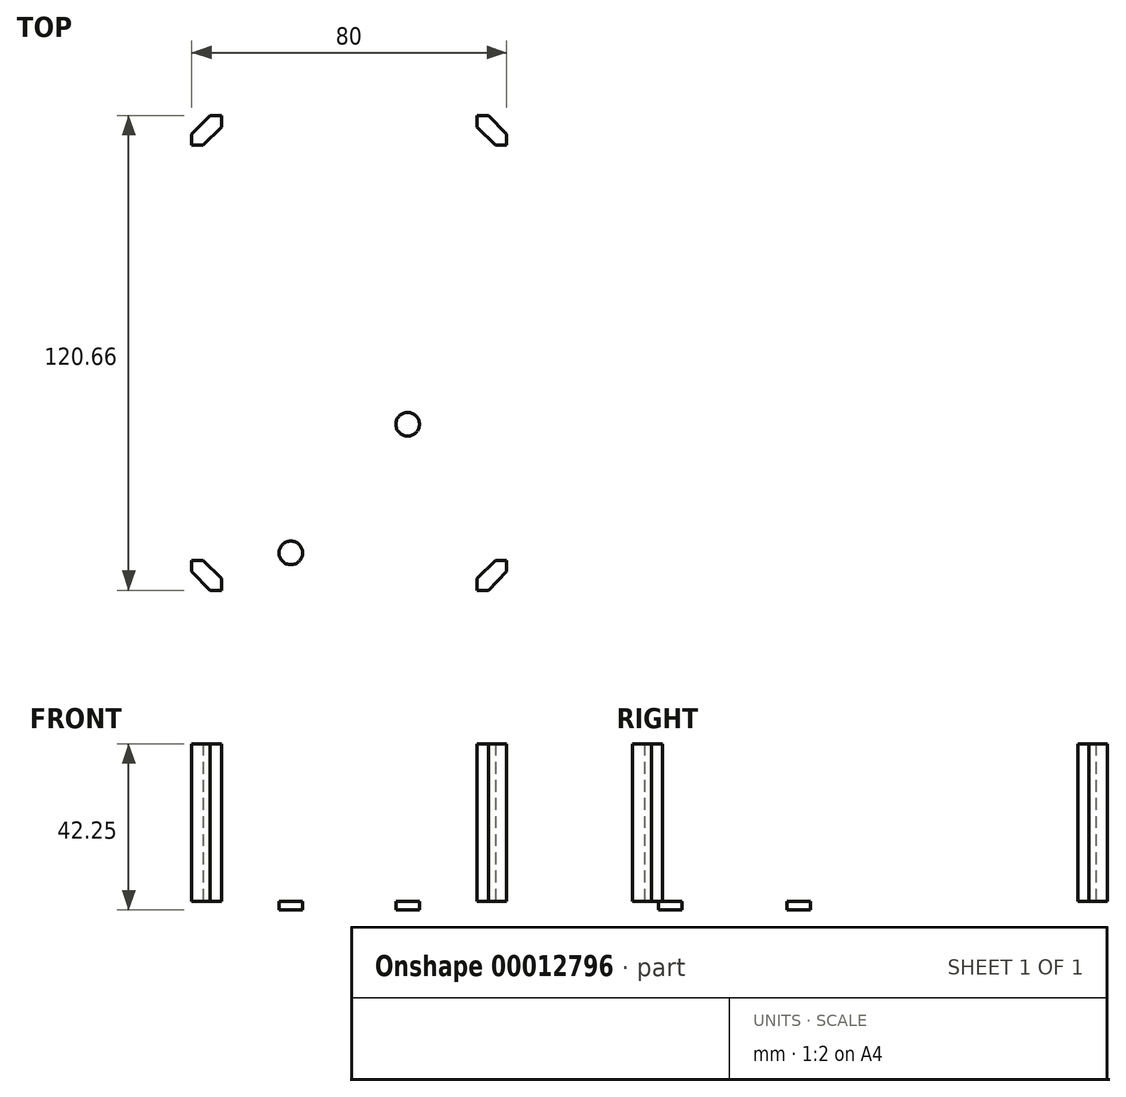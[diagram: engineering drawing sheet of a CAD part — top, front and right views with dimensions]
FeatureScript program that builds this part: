
annotation { "Feature Type Name" : "Feature", "Feature Type Description" : "" }
export const myFeature = defineFeature(function(context is Context, id is Id, definition is map)
    precondition{}
    {
        {
            var Q0;
            Q0=qCreatedBy(makeId("Top.planeOp"),FACE);
            var sketch = newSketch(context, id + "F0", { "sketchPlane" : qUnion([Q0])});
            skLineSegment(sketch, "E0.rect.bottom", {"start": v(-40, -60.33) * mm, "end": v(40, -60.33) * mm});
            skLineSegment(sketch, "E0.rect.top", {"start": v(-40, 60.33) * mm, "end": v(40, 60.33) * mm});
            skLineSegment(sketch, "E0.rect.left", {"start": v(-40, -60.33) * mm, "end": v(-40, 60.33) * mm});
            skLineSegment(sketch, "E0.rect.right", {"start": v(40, -60.33) * mm, "end": v(40, 60.33) * mm});
            skPoint(sketch, "E0.rect.middle", {"position": v(0, 0) * mm});
            skLineSegment(sketch, "E1", {"start": v(-35.41, 60.33) * mm, "end": v(-40, 55.6) * mm});
            skLineSegment(sketch, "E2", {"start": v(-35.22, -60.32) * mm, "end": v(-40, -55.8) * mm});
            skLineSegment(sketch, "E3.0.MirrorCS", {"start": v(35.22, -60.32) * mm, "end": v(40, -55.8) * mm});
            skLineSegment(sketch, "E4.0.MirrorCS", {"start": v(35.41, 60.33) * mm, "end": v(40, 55.6) * mm});
            skSolve(sketch);
        }
        {
            var Q0;
            {var subQ3=sQuery(id+"F0.wireOp",EDGE,"E1");Q0=makeQuery(id+"F0.imprint","IMPRINT",FACE,{"disambiguationData":[TD([[makeQuery(id+"F0.imprint","IMPRINT",EDGE,{"derivedFrom":subQ3}),1.0]])]});}
            extrude(context, id + "F1", {"entities" : qUnion([Q0]), "depth" : 2.25 * mm});
        }
        {
            var Q0;
            Q0=makeQuery(id+"F1.opExtrude","CAP_FACE",FACE,{"disambiguationData":[OSD([sQuery(id+"F0.wireOp",EDGE,"E0.rect.bottom"),sQuery(id+"F0.wireOp",EDGE,"E0.rect.top"),sQuery(id+"F0.wireOp",EDGE,"E0.rect.left"),sQuery(id+"F0.wireOp",EDGE,"E0.rect.right")])],"isStart":false});
            var sketch = newSketch(context, id + "F2", { "sketchPlane" : qUnion([Q0])});
            skCircle(sketch, "E5", {"center": v(-25, -34.48) * mm, "radius": 14.29 * mm, "construction": true});
            skCircle(sketch, "E6", {"center": v(-25, -34.48) * mm, "radius": 5.5 * mm});
            skCircle(sketch, "E7", {"center": v(-19.3, -16.1) * mm, "radius": 3 * mm});
            skCircle(sketch, "E8.0.MirrorC", {"center": v(-14.84, -50.82) * mm, "radius": 3 * mm});
            skLineSegment(sketch, "E9", {"start": v(-14.84, -50.82) * mm, "end": v(-19.3, -16.1) * mm, "construction": true});
            skLineSegment(sketch, "E10", {"start": v(-25, -34.48) * mm, "end": v(-17.07, -33.46) * mm, "construction": true});
            skCircle(sketch, "E11.1.0", {"center": v(25, -34.48) * mm, "radius": 5.5 * mm});
            skCircle(sketch, "E11.1.1", {"center": v(14.84, -18.14) * mm, "radius": 3 * mm});
            skCircle(sketch, "E11.1.2", {"center": v(19.3, -52.85) * mm, "radius": 3 * mm});
            skPoint(sketch, "E11.center", {"position": v(0, -34.48) * mm});
            skSolve(sketch);
        }
        {
            var Q0;
            Q0=makeQuery(id+"F2.imprint","IMPRINT",FACE,{"disambiguationData":[TD([[makeQuery(id+"F2.imprint","IMPRINT",EDGE,{"derivedFrom":sQuery(id+"F2.wireOp",EDGE,"E6")}),1.0]])]});
            var Q1;
            Q1=makeQuery(id+"F2.imprint","IMPRINT",FACE,{"disambiguationData":[TD([[makeQuery(id+"F2.imprint","IMPRINT",EDGE,{"derivedFrom":sQuery(id+"F2.wireOp",EDGE,"E7")}),1.0]])]});
            var Q2;
            Q2=makeQuery(id+"F2.imprint","IMPRINT",FACE,{"disambiguationData":[TD([[makeQuery(id+"F2.imprint","IMPRINT",EDGE,{"derivedFrom":sQuery(id+"F2.wireOp",EDGE,"E8.0.MirrorC")}),-1.0]])]});
            var Q3;
            Q3=makeQuery(id+"F2.imprint","IMPRINT",FACE,{"disambiguationData":[TD([[makeQuery(id+"F2.imprint","IMPRINT",EDGE,{"derivedFrom":sQuery(id+"F2.wireOp",EDGE,"E11.1.0")}),1.0]])]});
            var Q4;
            Q4=makeQuery(id+"F2.imprint","IMPRINT",FACE,{"disambiguationData":[TD([[makeQuery(id+"F2.imprint","IMPRINT",EDGE,{"derivedFrom":sQuery(id+"F2.wireOp",EDGE,"E11.1.2")}),1.0]])]});
            var Q5;
            Q5=makeQuery(id+"F2.imprint","IMPRINT",FACE,{"disambiguationData":[TD([[makeQuery(id+"F2.imprint","IMPRINT",EDGE,{"derivedFrom":sQuery(id+"F2.wireOp",EDGE,"E11.1.1")}),-1.0]])]});
            extrude(context, id + "F3", {"entities" : qUnion([Q0, Q1, Q2, Q3, Q4, Q5]), "operationType" : NewBodyOperationType.REMOVE, "oppositeDirection" : true, "depth" : 25.4 * mm});
        }
        {
            var Q0;
            Q0=makeQuery(id+"F1.opExtrude","CAP_FACE",FACE,{"disambiguationData":[OSD([sQuery(id+"F0.wireOp",EDGE,"E0.rect.bottom"),sQuery(id+"F0.wireOp",EDGE,"E0.rect.top"),sQuery(id+"F0.wireOp",EDGE,"E0.rect.left"),sQuery(id+"F0.wireOp",EDGE,"E0.rect.right")])],"isStart":true});
            var sketch = newSketch(context, id + "F4", { "sketchPlane" : qUnion([Q0])});
            skText(sketch, "E12", { "text": "HUGBOT", "fontName": "OpenSans-Bold.ttf"});
            const initialGuessF4  = {"E12": [-0.03225, -0.05059, 1, 0, 0.01068]};
            skSetInitialGuess(sketch, initialGuessF4);
            skSolve(sketch);
        }
        {
            var Q0;
            Q0=makeQuery(id+"F4.imprint","IMPRINT",FACE,{"disambiguationData":[TD([[makeQuery(id+"F4.imprint","IMPRINT",EDGE,{"derivedFrom":sQuery(id+"F4.wireOp",EDGE,"E12.sketch_text.stroke-71")}),-1.0]])]});
            var Q1;
            Q1=makeQuery(id+"F4.imprint","IMPRINT",FACE,{"disambiguationData":[TD([[makeQuery(id+"F4.imprint","IMPRINT",EDGE,{"derivedFrom":sQuery(id+"F4.wireOp",EDGE,"E12.sketch_text.stroke-85")}),-1.0]])]});
            var Q2;
            Q2=makeQuery(id+"F4.imprint","IMPRINT",FACE,{"disambiguationData":[TD([[makeQuery(id+"F4.imprint","IMPRINT",EDGE,{"derivedFrom":sQuery(id+"F4.wireOp",EDGE,"E12.sketch_text.stroke-46")}),-1.0]])]});
            var Q3;
            Q3=makeQuery(id+"F4.imprint","IMPRINT",FACE,{"disambiguationData":[TD([[makeQuery(id+"F4.imprint","IMPRINT",EDGE,{"derivedFrom":sQuery(id+"F4.wireOp",EDGE,"E12.sketch_text.stroke-27")}),-1.0]])]});
            var Q4;
            Q4=makeQuery(id+"F4.imprint","IMPRINT",FACE,{"disambiguationData":[TD([[makeQuery(id+"F4.imprint","IMPRINT",EDGE,{"derivedFrom":sQuery(id+"F4.wireOp",EDGE,"E12.sketch_text.stroke-12")}),-1.0]])]});
            var Q5;
            Q5=makeQuery(id+"F4.imprint","IMPRINT",FACE,{"disambiguationData":[TD([[makeQuery(id+"F4.imprint","IMPRINT",EDGE,{"derivedFrom":sQuery(id+"F4.wireOp",EDGE,"E12.sketch_text.stroke-0")}),-1.0]])]});
            extrude(context, id + "F5", {"entities" : qUnion([Q0, Q1, Q2, Q3, Q4, Q5]), "operationType" : NewBodyOperationType.REMOVE, "oppositeDirection" : true, "depth" : .3 * mm});
        }
        {
            var Q0;
            Q0=makeQuery(id+"F1.opExtrude","CAP_FACE",FACE,{"disambiguationData":[OSD([sQuery(id+"F0.wireOp",EDGE,"E0.rect.bottom"),sQuery(id+"F0.wireOp",EDGE,"E0.rect.top"),sQuery(id+"F0.wireOp",EDGE,"E0.rect.left"),sQuery(id+"F0.wireOp",EDGE,"E0.rect.right"),sQuery(id+"F0.wireOp",EDGE,"E1"),sQuery(id+"F0.wireOp",EDGE,"E2")])],"isStart":false});
            var sketch = newSketch(context, id + "F6", { "sketchPlane" : qUnion([Q0])});
            skLineSegment(sketch, "E13", {"start": v(-32.45, 60.33) * mm, "end": v(-32.45, 57.36) * mm});
            skLineSegment(sketch, "E14", {"start": v(-32.45, 57.36) * mm, "end": v(-37.17, 52.78) * mm});
            skLineSegment(sketch, "E15", {"start": v(-37.17, 52.78) * mm, "end": v(-40, 52.78) * mm});
            skLineSegment(sketch, "E16", {"start": v(-32.45, 60.33) * mm, "end": v(-35.41, 60.33) * mm});
            skLineSegment(sketch, "E17", {"start": v(-40, 55.6) * mm, "end": v(-35.41, 60.33) * mm});
            skLineSegment(sketch, "E18", {"start": v(-40, 52.78) * mm, "end": v(-40, 55.6) * mm});
            skLineSegment(sketch, "E19.0.MirrorCS", {"start": v(32.45, 60.33) * mm, "end": v(35.41, 60.33) * mm});
            skLineSegment(sketch, "E20.0.MirrorCS", {"start": v(32.45, 57.36) * mm, "end": v(37.17, 52.78) * mm});
            skLineSegment(sketch, "E21.0.MirrorCS", {"start": v(37.17, 52.78) * mm, "end": v(40, 52.78) * mm});
            skLineSegment(sketch, "E22.0.MirrorCS", {"start": v(32.45, 60.33) * mm, "end": v(32.45, 57.36) * mm});
            skLineSegment(sketch, "E23.0.MirrorCS", {"start": v(40, 55.6) * mm, "end": v(35.41, 60.33) * mm});
            skLineSegment(sketch, "E24.0.MirrorCS", {"start": v(40, 52.78) * mm, "end": v(40, 55.6) * mm});
            skLineSegment(sketch, "E25.0.MirrorCS", {"start": v(-40, -52.78) * mm, "end": v(-40, -55.6) * mm});
            skLineSegment(sketch, "E25.1.MirrorCS", {"start": v(-32.45, -60.33) * mm, "end": v(-35.41, -60.33) * mm});
            skLineSegment(sketch, "E25.2.MirrorCS", {"start": v(-40, -55.6) * mm, "end": v(-35.41, -60.33) * mm});
            skLineSegment(sketch, "E25.3.MirrorCS", {"start": v(-32.45, -57.36) * mm, "end": v(-37.17, -52.78) * mm});
            skLineSegment(sketch, "E26.0.MirrorCS", {"start": v(-37.17, -52.78) * mm, "end": v(-40, -52.78) * mm});
            skLineSegment(sketch, "E26.4.MirrorCS", {"start": v(-32.45, -60.33) * mm, "end": v(-32.45, -57.36) * mm});
            skLineSegment(sketch, "E27.0.MirrorCS", {"start": v(32.45, -60.33) * mm, "end": v(32.45, -57.36) * mm});
            skLineSegment(sketch, "E27.1.MirrorCS", {"start": v(40, -55.6) * mm, "end": v(35.41, -60.33) * mm});
            skLineSegment(sketch, "E27.2.MirrorCS", {"start": v(32.45, -60.33) * mm, "end": v(35.41, -60.33) * mm});
            skLineSegment(sketch, "E27.3.MirrorCS", {"start": v(40, -52.78) * mm, "end": v(40, -55.6) * mm});
            skLineSegment(sketch, "E27.4.MirrorCS", {"start": v(37.17, -52.78) * mm, "end": v(40, -52.78) * mm});
            skLineSegment(sketch, "E27.5.MirrorCS", {"start": v(32.45, -57.36) * mm, "end": v(37.17, -52.78) * mm});
            skSolve(sketch);
        }
        {
            var Q0;
            Q0 = qSketchRegion(id + "F6", true);
            extrude(context, id + "F7", {"entities" : qUnion([Q0]), "operationType" : NewBodyOperationType.ADD, "depth" : 40 * mm});
        }
    });
